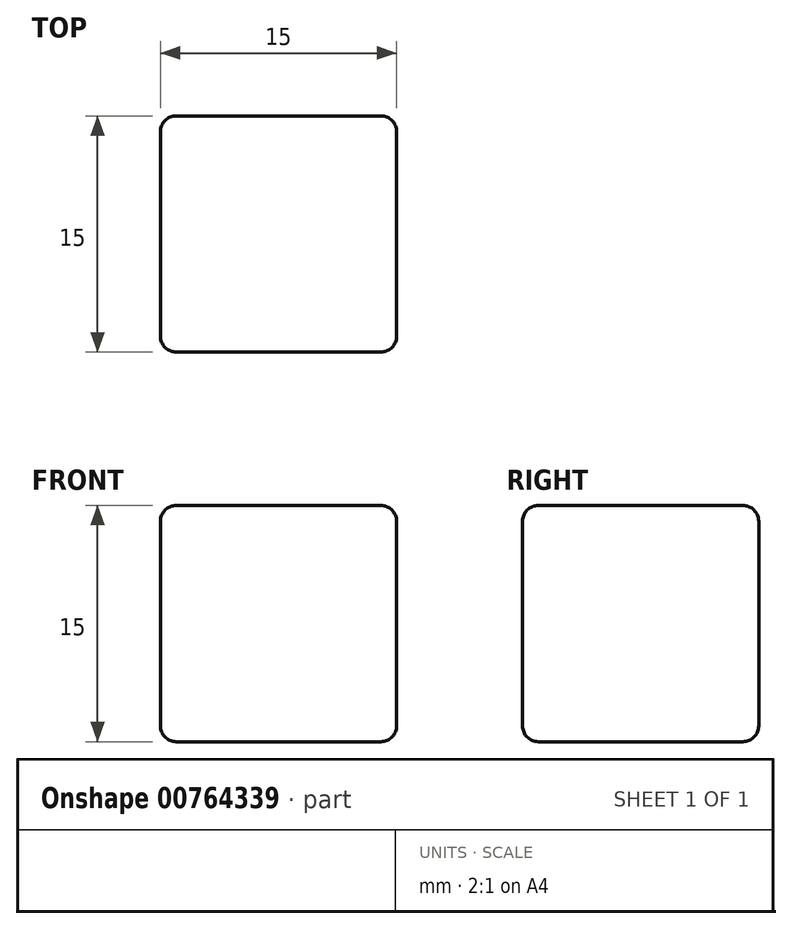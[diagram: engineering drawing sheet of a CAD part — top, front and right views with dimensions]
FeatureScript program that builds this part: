
annotation { "Feature Type Name" : "Feature", "Feature Type Description" : "" }
export const myFeature = defineFeature(function(context is Context, id is Id, definition is map)
    precondition{}
    {
        {
            var Q0;
            Q0=qCreatedBy(makeId("Top.planeOp"),FACE);
            var sketch = newSketch(context, id + "F0", { "sketchPlane" : qUnion([Q0])});
            skLineSegment(sketch, "E0.bottom", {"start": v(-7.5, 7.5) * mm, "end": v(7.5, 7.5) * mm});
            skLineSegment(sketch, "E0.top", {"start": v(-7.5, -7.5) * mm, "end": v(7.5, -7.5) * mm});
            skLineSegment(sketch, "E0.left", {"start": v(-7.5, 7.5) * mm, "end": v(-7.5, -7.5) * mm});
            skLineSegment(sketch, "E0.right", {"start": v(7.5, 7.5) * mm, "end": v(7.5, -7.5) * mm});
            skPoint(sketch, "E0.middle", {"position": v(0, 0) * mm});
            skSolve(sketch);
        }
        {
            var Q0;
            Q0=makeQuery(id+"F0.imprint","IMPRINT",FACE,{"disambiguationData":[TD([[makeQuery(id+"F0.imprint","IMPRINT",EDGE,{"derivedFrom":sQuery(id+"F0.wireOp",EDGE,"E0.bottom")}),-1.0]])]});
            extrude(context, id + "F1", {"entities" : qUnion([Q0]), "endBound" : BoundingType.SYMMETRIC, "depth" : 15 * mm, "offsetDistance" : 25 * mm});
        }
        {
            var Q0;
            Q0=makeQuery(id+"F1.opExtrude","SWEPT_FACE",FACE,{"disambiguationData":[OSD([sQuery(id+"F0.wireOp",EDGE,"E0.top")])]});
            var Q1;
            Q1=makeQuery(id+"F1.opExtrude","SWEPT_FACE",FACE,{"disambiguationData":[OSD([sQuery(id+"F0.wireOp",EDGE,"E0.right")])]});
            var Q2;
            Q2=makeQuery(id+"F1.opExtrude","CAP_FACE",FACE,{"disambiguationData":[OSD([sQuery(id+"F0.wireOp",EDGE,"E0.bottom"),sQuery(id+"F0.wireOp",EDGE,"E0.top"),sQuery(id+"F0.wireOp",EDGE,"E0.left"),sQuery(id+"F0.wireOp",EDGE,"E0.right")])],"isStart":false});
            var Q3;
            Q3=makeQuery(id+"F1.opExtrude","SWEPT_FACE",FACE,{"disambiguationData":[OSD([sQuery(id+"F0.wireOp",EDGE,"E0.left")])]});
            var Q4;
            Q4=makeQuery(id+"F1.opExtrude","CAP_FACE",FACE,{"disambiguationData":[OSD([sQuery(id+"F0.wireOp",EDGE,"E0.bottom"),sQuery(id+"F0.wireOp",EDGE,"E0.top"),sQuery(id+"F0.wireOp",EDGE,"E0.left"),sQuery(id+"F0.wireOp",EDGE,"E0.right")])],"isStart":true});
            var Q5;
            Q5=makeQuery(id+"F1.opExtrude","SWEPT_FACE",FACE,{"disambiguationData":[OSD([sQuery(id+"F0.wireOp",EDGE,"E0.bottom")])]});
            fillet(context, id + "F2", {"entities" : qUnion([Q0, Q1, Q2, Q3, Q4, Q5]), "radius" : 1 * mm, "tangentPropagation" : true, "allowEdgeOverflow" : false});
        }
    });
